# Revit family: IS_Tesi_A6566_BIM_IT
name_source: partatom
category: Plumbing Fixtures
revit_build: Autodesk Revit 2017 (Build: 20160225_1515(x64)
units: mm (PartAtom-declared; Revit-internal decimal feet)

## family parameters
Always vertical = No
Cut with Voids When Loaded = No
OmniClass Number = 23.45.55.17
OmniClass Title = Mixing Faucets
Part Type = Normal
Room Calculation Point = No
Round Connector Dimension = Use Diameter
Shared = No
Work Plane-Based = No

## types (1)
- A6566AA - TESI PICCOLO single lever basin mixer with pop-up waste
    Accessori = www.idealstandard.it
    AltezzaNominale = 124 mm
    BIMobject category = Taps & Mixers
    BIMobject category code = sanitary-taps-mixers
    BIMobject main category = Sanitary
    BIMobject main category code = sanitary
    BOSUseNativeGeometries = 1
    Brand = Ideal Standard
    Brand url = http://www.idealstandard.it
    Caratteristiche = TESI BSN MXR RMTD CHR PICC PU/M 5L/MIN
    CodiceABarre = 4015413338301
    CodiceDiPrestazione = EN
    Colore = Cromo
    Connessione = piombatura
    CostoDiSostituzione = 0 $
    Date of publishing = 2019_01_04
    Description = TESI BSN MXR RMTD CHR PICC PU/M 5L/MIN
    Desrizione = TESI BSN MXR RMTD CHR PICC PU/M 5L/MIN
    Dimensione = 50 x 139 x 124mm
    DimensioneScarico = 0
    EAN code = https://4015413338301
    Edition number = 1
    Finitura = Cromo
    Forma = scolpito
    Garanzia = Garanzia Ideal Standard
    GaranziaInstallazione = n/s
    Grado = n/s
    IFC Classification = IfcSanitaryTerminal
    IfcEsportaCome = SanitaryTerminal
    InformazioniDiProdotto = http://www.idealstandard.it
    Installation instructions = http://www.idealstandard.it
    Installazione = http://www.idealstandard.it
    InstruzioniInstallazione = http://www.idealstandard.it
    LarghezzaNominale = 0 mm  [stored 0 ft]
    LunghezzaNominale = 138 mm
    Maniglia = No
    Manufacturer name = Ideal Standard
    Material main = Brass
    Materiale = Ottone
    Model = A6566AA
    NBS Reference Code = Pr_40_20_87_98
    NBS Reference Description = Washbasin taps
    Nominal depth = 0
    Nominal height = 0
    NominalHeight = 124 mm
    NominalLength = 138 mm
    NominalWidth = 50 mm  [stored 0.164042 ft]
    NumeroDiModello = K079401
    OmniClass Code = 23-31 11 00
    OmniClass Description = Faucets
    PartiDiRicambio = http://www.idealstandard.it
    PiattoDoccia = No
    Product Guid = 91c6d9a1-7d18-4fa8-be1a-d404f9b0d237
    Product SKU = A6566
    Product certification = http://www.idealstandard.it
    Product data url = https://bimobject.com
    Product family = TESI
    Product group = Basin Mixer
    Product name = TESI PICCOLO single lever basin mixer with pop-up waste
    Product url = http://www.idealstandard.it
    ProfonditaNominale = 0 mm  [stored 0 ft]
    QR code = http://bimobject.com
    Revisione = 1
    SeatMaterial = 0 mm  [stored 0 ft]
    Size = 124 x 138 x 50mm
    SpessoreDelMateriale = 0
    SpilloverLivello = 0
    Technical description = http://www.idealstandard.it
    Telefono = 800 652 290
    TipoDiDato = Fisso
    TipoEspotazioneIfc = IfcSanitaryTerminalType
    URL = http://www.idealstandard.it
    Uniclass 1.4 Code = L8212
    Uniclass 1.4 Description = Fittings
    Uniclass 2.0 Code = PR-35-79-95
    Uniclass 2.0 Description = Wash Basin And Trough Water Supply Fittings
    Uniclass 2015 Code = Pr_40_20_87_96
    Uniclass 2015 Name = Washbasin manual water supply sets
    UnitàDurata = anni
    UnitàDurataGaranzia = anni
    UnitàLineare = millimetri
    UnitàMonetaria = €
    UnitàSuperficie = €
    UnitàVolume = millimetri
    Versione = 1
    VersioneClassificazioneUni2015 = 1
    Weight Net (Kg) = 0
    Youtube clip = https://www.youtube.com

note: [stored X ft] marks values corroborated as IEEE doubles in the binary element streams (Revit-internal decimal feet)

## geometry (parser evidence)
native form markers: Sweep x2
no freeform markers — native parametric forms only
